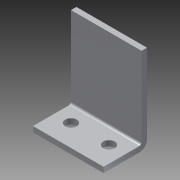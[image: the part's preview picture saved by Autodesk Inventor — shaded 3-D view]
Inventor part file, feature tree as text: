
AUTODESK INVENTOR PART (.ipt)
format: ipt  version: 2013 (Build 170138000, 138)  size: 150,016 bytes
history: native  units: in
note: dims shown in document units (in); Inventor stores cm internally (conversion verified against a paired STEP export)
features: sheet_metal_op x4, other x4, sketch x2
ambient origin geometry x8: Origin, YZ Plane, XZ Plane, XY Plane, X Axis, Y Axis, Z Axis, Center Point
bodies: Solid1 (feature_tree)
feature tree (10):
  sheet_metal_op  "Face1"
  sheet_metal_op  "Flange1"
  sketch  "Sketch1"  dims[d0=1.0in]
  other  "Plate1"
  sketch  "Sketch2"  dims[d2=0.266in d3=0.266in d4=0.875in d5=0.375in d6=0.375in d7=0.5in d8=0.5in d9=0.125in d10=0.125in d11=0.0625in d12=0.25in d13=0.125in d14=2.0in d15=90.0deg d16=0.05in d17=0.5in d18=0.125in d19=0.125in d1=0.125in]
  other  "Plate2"
  sheet_metal_op  "Bend1"
  sheet_metal_op  "Corner1"
  other  "Definition1"
  other  "Cut1"
